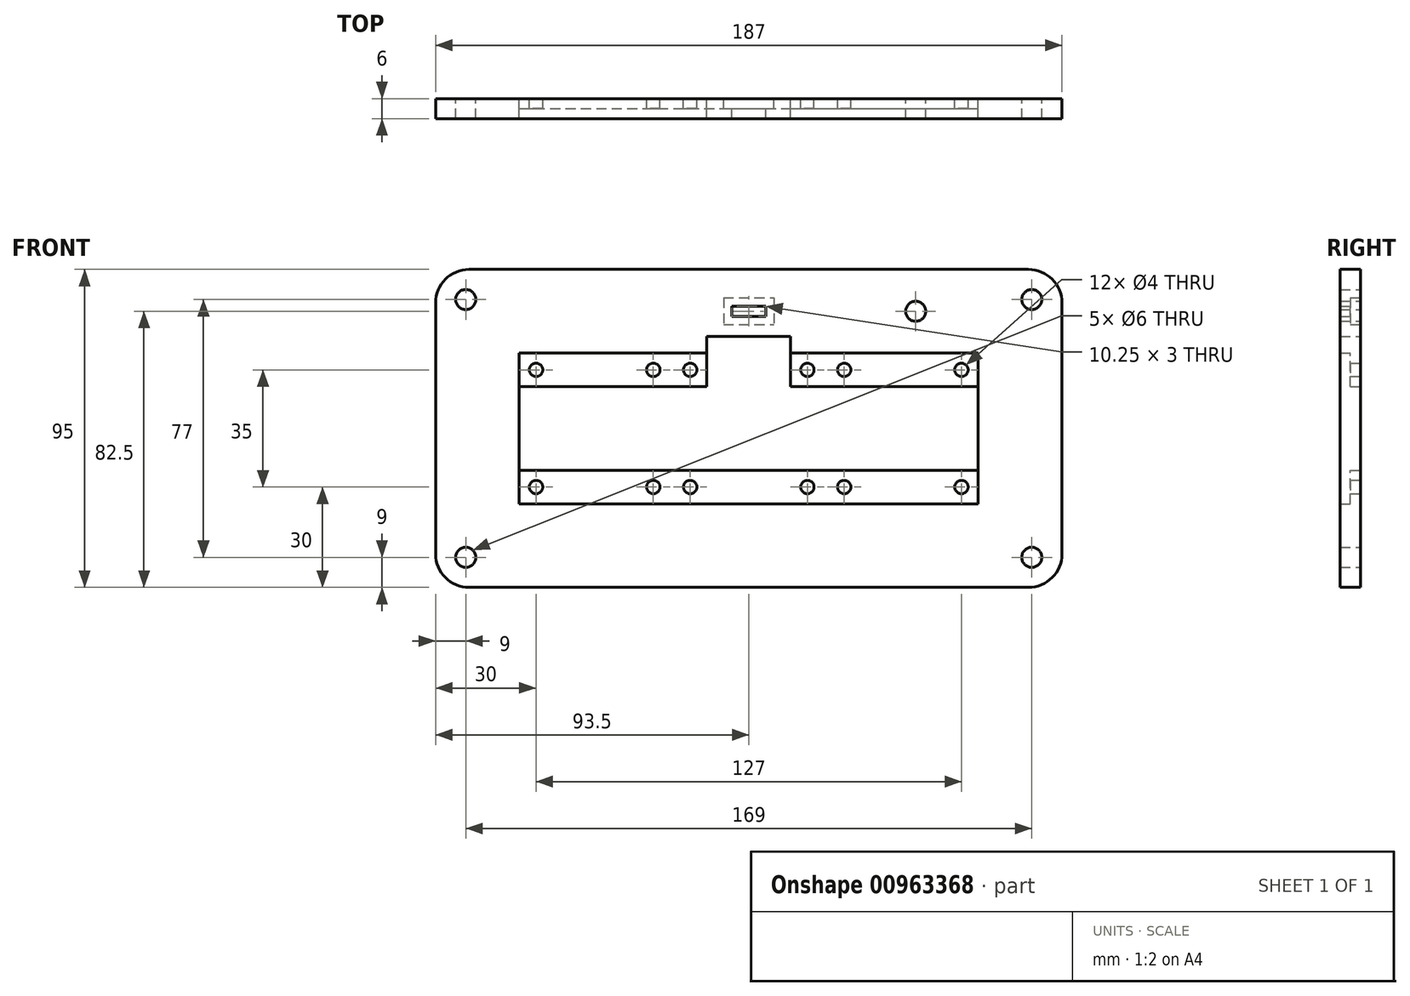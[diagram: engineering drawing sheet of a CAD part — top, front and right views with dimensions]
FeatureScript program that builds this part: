
annotation { "Feature Type Name" : "Feature", "Feature Type Description" : "" }
export const myFeature = defineFeature(function(context is Context, id is Id, definition is map)
    precondition{}
    {
        {
            var Q0;
            Q0=qCreatedBy(makeId("Front.planeOp"),FACE);
            var sketch = newSketch(context, id + "F0", { "sketchPlane" : qUnion([Q0])});
            skLineSegment(sketch, "E0.bottom", {"start": v(68.5, 22.5) * mm, "end": v(-68.5, 22.5) * mm});
            skLineSegment(sketch, "E0.top", {"start": v(68.5, -22.5) * mm, "end": v(-68.5, -22.5) * mm});
            skLineSegment(sketch, "E0.left", {"start": v(68.5, 22.5) * mm, "end": v(68.5, -22.5) * mm});
            skLineSegment(sketch, "E0.right", {"start": v(-68.5, 22.5) * mm, "end": v(-68.5, -22.5) * mm});
            skPoint(sketch, "E0.middle", {"position": v(0, 0) * mm});
            skLineSegment(sketch, "E1.bottom", {"start": v(93.5, 47.5) * mm, "end": v(-93.5, 47.5) * mm});
            skLineSegment(sketch, "E1.top", {"start": v(93.5, -47.5) * mm, "end": v(-93.5, -47.5) * mm});
            skLineSegment(sketch, "E1.left", {"start": v(93.5, 47.5) * mm, "end": v(93.5, -47.5) * mm});
            skLineSegment(sketch, "E1.right", {"start": v(-93.5, 47.5) * mm, "end": v(-93.5, -47.5) * mm});
            skCircle(sketch, "E2", {"center": v(-84.5, 38.5) * mm, "radius": 3 * mm});
            skCircle(sketch, "E3", {"center": v(84.5, 38.5) * mm, "radius": 3 * mm});
            skCircle(sketch, "E4", {"center": v(84.5, -38.5) * mm, "radius": 3 * mm});
            skCircle(sketch, "E5", {"center": v(-84.5, -38.5) * mm, "radius": 3 * mm});
            skLineSegment(sketch, "E6.bottom", {"start": v(84.5, 38.5) * mm, "end": v(-84.5, 38.5) * mm, "construction": true});
            skLineSegment(sketch, "E6.top", {"start": v(84.5, -38.5) * mm, "end": v(-84.5, -38.5) * mm, "construction": true});
            skLineSegment(sketch, "E6.left", {"start": v(84.5, 38.5) * mm, "end": v(84.5, -38.5) * mm, "construction": true});
            skLineSegment(sketch, "E6.right", {"start": v(-84.5, 38.5) * mm, "end": v(-84.5, -38.5) * mm, "construction": true});
            skLineSegment(sketch, "E7.bottom", {"start": v(5.12, 36.5) * mm, "end": v(-5.12, 36.5) * mm});
            skLineSegment(sketch, "E7.top", {"start": v(5.12, 33.5) * mm, "end": v(-5.12, 33.5) * mm});
            skLineSegment(sketch, "E7.left", {"start": v(5.12, 36.5) * mm, "end": v(5.12, 33.5) * mm});
            skLineSegment(sketch, "E7.right", {"start": v(-5.12, 36.5) * mm, "end": v(-5.12, 33.5) * mm});
            skPoint(sketch, "E7.middle", {"position": v(0, 35) * mm});
            skPoint(sketch, "E7.middle.positionSnap0", {"position": v(0, 38.5) * mm});
            skPoint(sketch, "E7.centerSnap0", {"position": v(0, 38.5) * mm});
            skCircle(sketch, "E8", {"center": v(49.83, 35) * mm, "radius": 3 * mm});
            skLineSegment(sketch, "E9.bottom", {"start": v(12.5, 27.5) * mm, "end": v(-12.5, 27.5) * mm});
            skLineSegment(sketch, "E9.top", {"start": v(12.5, 17.5) * mm, "end": v(-12.5, 17.5) * mm});
            skLineSegment(sketch, "E9.left", {"start": v(12.5, 27.5) * mm, "end": v(12.5, 17.5) * mm});
            skLineSegment(sketch, "E9.right", {"start": v(-12.5, 27.5) * mm, "end": v(-12.5, 17.5) * mm});
            skPoint(sketch, "E9.middle", {"position": v(0, 22.5) * mm});
            skSolve(sketch);
        }
        {
            var Q0;
            Q0 = qSketchRegion(id + "F0", true);
            extrude(context, id + "F1", {"entities" : qUnion([Q0]), "depth" : 6 * mm, "offsetDistance" : 25 * mm});
        }
        {
            var Q0;
            Q0=makeQuery(id+"F1.opExtrude","SWEPT_EDGE",EDGE,{"disambiguationData":[OSD([sQuery(id+"F0.wireOp",EDGE,"E1.top"),sQuery(id+"F0.wireOp",EDGE,"E1.left")])]});
            var Q1;
            Q1=makeQuery(id+"F1.opExtrude","SWEPT_EDGE",EDGE,{"disambiguationData":[OSD([sQuery(id+"F0.wireOp",EDGE,"E1.top"),sQuery(id+"F0.wireOp",EDGE,"E1.right")])]});
            var Q2;
            Q2=makeQuery(id+"F1.opExtrude","SWEPT_EDGE",EDGE,{"disambiguationData":[OSD([sQuery(id+"F0.wireOp",EDGE,"E1.bottom"),sQuery(id+"F0.wireOp",EDGE,"E1.right")])]});
            var Q3;
            Q3=makeQuery(id+"F1.opExtrude","SWEPT_EDGE",EDGE,{"disambiguationData":[OSD([sQuery(id+"F0.wireOp",EDGE,"E1.bottom"),sQuery(id+"F0.wireOp",EDGE,"E1.left")])]});
            fillet(context, id + "F2", {"entities" : qUnion([Q0, Q1, Q2, Q3]), "radius" : 10 * mm, "tangentPropagation" : true, "allowEdgeOverflow" : false});
        }
        {
            var Q0;
            Q0=makeQuery(id+"F1.opExtrude","CAP_FACE",FACE,{"disambiguationData":[OSD([sQuery(id+"F0.wireOp",EDGE,"E0.bottom"),sQuery(id+"F0.wireOp",EDGE,"E0.top"),sQuery(id+"F0.wireOp",EDGE,"E0.left"),sQuery(id+"F0.wireOp",EDGE,"E0.right"),sQuery(id+"F0.wireOp",EDGE,"E1.bottom"),sQuery(id+"F0.wireOp",EDGE,"E1.top"),sQuery(id+"F0.wireOp",EDGE,"E1.left"),sQuery(id+"F0.wireOp",EDGE,"E1.right"),sQuery(id+"F0.wireOp",EDGE,"E2"),sQuery(id+"F0.wireOp",EDGE,"E3"),sQuery(id+"F0.wireOp",EDGE,"E4"),sQuery(id+"F0.wireOp",EDGE,"E5"),sQuery(id+"F0.wireOp",EDGE,"E7.bottom"),sQuery(id+"F0.wireOp",EDGE,"E7.top"),sQuery(id+"F0.wireOp",EDGE,"E7.left"),sQuery(id+"F0.wireOp",EDGE,"E7.right"),sQuery(id+"F0.wireOp",EDGE,"E8"),sQuery(id+"F0.wireOp",EDGE,"E9.bottom"),sQuery(id+"F0.wireOp",EDGE,"E9.left"),sQuery(id+"F0.wireOp",EDGE,"E9.right")])],"isStart":true});
            var sketch = newSketch(context, id + "F3", { "sketchPlane" : qUnion([Q0])});
            skLineSegment(sketch, "E10", {"start": v(-5.12, 36.5) * mm, "end": v(5.12, 33.5) * mm, "construction": true});
            skLineSegment(sketch, "E11.bottom", {"start": v(7.5, 39) * mm, "end": v(-7.5, 39) * mm});
            skLineSegment(sketch, "E11.top", {"start": v(7.5, 31) * mm, "end": v(-7.5, 31) * mm});
            skLineSegment(sketch, "E11.left", {"start": v(7.5, 39) * mm, "end": v(7.5, 31) * mm});
            skLineSegment(sketch, "E11.right", {"start": v(-7.5, 39) * mm, "end": v(-7.5, 31) * mm});
            skPoint(sketch, "E11.middle", {"position": v(0, 35) * mm});
            skSolve(sketch);
        }
        {
            var Q0;
            Q0 = qSketchRegion(id + "F3", true);
            extrude(context, id + "F4", {"entities" : qUnion([Q0]), "operationType" : NewBodyOperationType.REMOVE, "oppositeDirection" : true, "depth" : 3 * mm, "offsetDistance" : 25 * mm});
        }
        {
            var Q0;
            Q0=makeQuery(id+"F1.opExtrude","CAP_FACE",FACE,{"disambiguationData":[OSD([sQuery(id+"F0.wireOp",EDGE,"E0.bottom"),sQuery(id+"F0.wireOp",EDGE,"E0.top"),sQuery(id+"F0.wireOp",EDGE,"E0.left"),sQuery(id+"F0.wireOp",EDGE,"E0.right"),sQuery(id+"F0.wireOp",EDGE,"E1.bottom"),sQuery(id+"F0.wireOp",EDGE,"E1.top"),sQuery(id+"F0.wireOp",EDGE,"E1.left"),sQuery(id+"F0.wireOp",EDGE,"E1.right"),sQuery(id+"F0.wireOp",EDGE,"E2"),sQuery(id+"F0.wireOp",EDGE,"E3"),sQuery(id+"F0.wireOp",EDGE,"E4"),sQuery(id+"F0.wireOp",EDGE,"E5"),sQuery(id+"F0.wireOp",EDGE,"E7.bottom"),sQuery(id+"F0.wireOp",EDGE,"E7.top"),sQuery(id+"F0.wireOp",EDGE,"E7.left"),sQuery(id+"F0.wireOp",EDGE,"E7.right"),sQuery(id+"F0.wireOp",EDGE,"E8"),sQuery(id+"F0.wireOp",EDGE,"E9.bottom"),sQuery(id+"F0.wireOp",EDGE,"E9.left"),sQuery(id+"F0.wireOp",EDGE,"E9.right")])],"isStart":true});
            var sketch = newSketch(context, id + "F5", { "sketchPlane" : qUnion([Q0])});
            skLineSegment(sketch, "E12", {"start": v(-12.5, 22.5) * mm, "end": v(-12.5, 12.5) * mm});
            skLineSegment(sketch, "E13", {"start": v(-12.5, 12.5) * mm, "end": v(-68.5, 12.5) * mm});
            skLineSegment(sketch, "E14", {"start": v(-68.5, 12.5) * mm, "end": v(-75.94, 12.5) * mm});
            skLineSegment(sketch, "E15", {"start": v(-75.94, 12.5) * mm, "end": v(-75.94, 27.85) * mm});
            skLineSegment(sketch, "E16", {"start": v(-75.94, 27.85) * mm, "end": v(-12.5, 27.5) * mm});
            skLineSegment(sketch, "E17", {"start": v(-12.5, 27.5) * mm, "end": v(-12.5, 22.5) * mm});
            skLineSegment(sketch, "E18", {"start": v(12.5, 22.5) * mm, "end": v(12.5, 12.5) * mm});
            skLineSegment(sketch, "E19", {"start": v(12.5, 12.5) * mm, "end": v(71.99, 12.5) * mm});
            skLineSegment(sketch, "E20", {"start": v(71.99, 12.5) * mm, "end": v(71.99, 27.85) * mm});
            skLineSegment(sketch, "E21", {"start": v(71.99, 27.85) * mm, "end": v(12.5, 22.5) * mm});
            skLineSegment(sketch, "E22", {"start": v(-68.5, -12.5) * mm, "end": v(72.55, -12.5) * mm});
            skLineSegment(sketch, "E23", {"start": v(72.55, -12.5) * mm, "end": v(72.55, -24.07) * mm});
            skLineSegment(sketch, "E24", {"start": v(72.55, -24.07) * mm, "end": v(-76.5, -24.07) * mm});
            skLineSegment(sketch, "E25", {"start": v(-76.5, -24.07) * mm, "end": v(-73.25, -11.94) * mm});
            skLineSegment(sketch, "E26", {"start": v(-68.5, -12.5) * mm, "end": v(-73.25, -11.94) * mm});
            skCircle(sketch, "E27", {"center": v(-63.5, 17.5) * mm, "radius": 2 * mm});
            skCircle(sketch, "E28", {"center": v(-17.5, 17.5) * mm, "radius": 2 * mm});
            skCircle(sketch, "E29", {"center": v(-28.5, 17.5) * mm, "radius": 2 * mm});
            skCircle(sketch, "E30", {"center": v(17.5, 17.5) * mm, "radius": 2 * mm});
            skCircle(sketch, "E31", {"center": v(28.5, 17.5) * mm, "radius": 2 * mm});
            skCircle(sketch, "E32", {"center": v(63.5, 17.5) * mm, "radius": 2 * mm});
            skCircle(sketch, "E33", {"center": v(63.5, -17.5) * mm, "radius": 2 * mm});
            skCircle(sketch, "E34", {"center": v(28.5, -17.5) * mm, "radius": 2 * mm});
            skCircle(sketch, "E35", {"center": v(17.5, -17.5) * mm, "radius": 2 * mm});
            skCircle(sketch, "E36", {"center": v(-17.5, -17.5) * mm, "radius": 2 * mm});
            skCircle(sketch, "E37", {"center": v(-28.5, -17.5) * mm, "radius": 2 * mm});
            skCircle(sketch, "E38", {"center": v(-63.5, -17.5) * mm, "radius": 2 * mm});
            skSolve(sketch);
        }
        {
            var Q0;
            Q0 = qSketchRegion(id + "F5", true);
            extrude(context, id + "F6", {"entities" : qUnion([Q0]), "operationType" : NewBodyOperationType.ADD, "oppositeDirection" : true, "depth" : 3 * mm, "offsetDistance" : 25 * mm});
        }
    });
